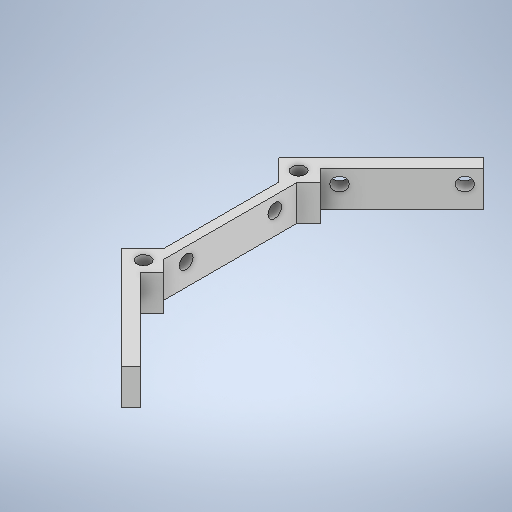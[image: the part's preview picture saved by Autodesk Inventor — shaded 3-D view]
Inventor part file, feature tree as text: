
AUTODESK INVENTOR PART (.ipt)
format: ipt  version: 2025.1 (Build 291241020, 241B)  size: 314,368 bytes
history: native  units: in
note: dims shown in document units (in); Inventor stores cm internally (conversion verified against a paired STEP export)
features: sketch x5, extrude x4
ambient origin geometry x8: Origin, YZ Plane, XZ Plane, XY Plane, X Axis, Y Axis, Z Axis, Center Point
bodies: Body1 (feature_tree)
feature tree (9):
  extrude  "Extrusion2"  Depth=0.9843in
  sketch  "Sketch3"  dims[d8=0.5118in d9=1.0236in]
  extrude  "Extrusion3"  Depth=1.0236in
  extrude  "Extrusion4"  Depth=0.1181in
  extrude  "Extrusion5"  Depth=1.0236in
  sketch  "Sketch1"  dims[d3=0.9843in d6=0.9843in]
  sketch  "Sketch4"  dims[d10=0.1181in d12=0.1201in]
  sketch  "Sketch5"  dims[d13=0.1201in d16=1.0236in]
  sketch  "Sketch6"  dims[d17=135.0deg d18=0.315in d19=0.0in d20=0.1969in d21=0.3937in d22=0.7874in d23=0.122in d24=0.122in d25=0.315in d26=0.0in d27=0.1969in d28=0.3937in d29=0.7874in d30=0.122in d31=0.122in d32=0.315in d33=0.0in d34=1.0236in d35=0.5118in d36=0.1969in d37=0.3937in d38=0.7874in d39=0.122in d40=0.122in d41=0.315in d42=0.0in d14=0.0197in d15=0.0344in]
